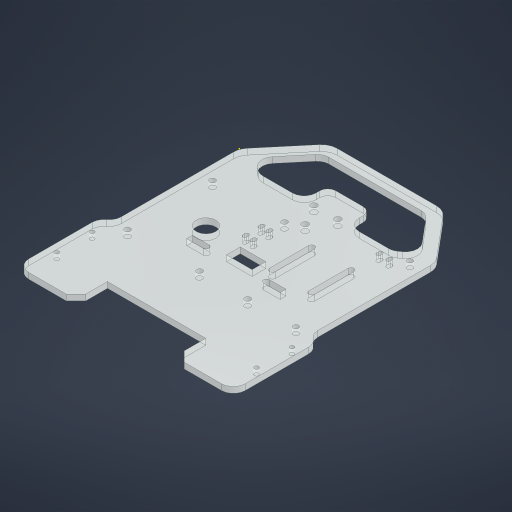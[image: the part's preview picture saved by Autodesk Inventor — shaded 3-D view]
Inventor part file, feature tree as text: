
AUTODESK INVENTOR PART (.ipt)
format: ipt  version: 2023 (Build 270158000, 158)  size: 454,656 bytes
history: native  units: mm
features: sketch x3, extrude x2, fillet x1, chamfer x1
ambient origin geometry x8: Origin, YZ Plane, XZ Plane, XY Plane, X Axis, Y Axis, Z Axis, Center Point
bodies: Solid1 (feature_tree)
feature tree (7):
  extrude  "Extrusion1"  Depth=100.0mm
  fillet  "Fillet1"  Radius=8.0mm
  sketch  "Sketch2"  dims[d4=2.2mm d5=18.0mm]
  extrude  "Extrusion2"  Depth=18.0mm
  chamfer  "Chamfer2"  Distance=36.576mm
  sketch  "Sketch1"  dims[d0=100.0mm d1=100.0mm d2=8.0mm]
  sketch  "Sketch3"  dims[d6=43.18mm d7=36.576mm d8=3.0mm d9=49.0mm d10=58.0mm d15=2.75mm d27=3.0mm d28=0.0mm d33=22.0mm d34=25.0mm d36=22.68928mm d37=6.0mm d38=6.0mm d39=12.0mm d40=6.0mm d41=8.0mm d44=2.3mm d45=13.462mm d46=5.0mm d47=14.0mm d48=15.5mm d49=3.3mm d54=4.0mm d55=5.0mm d56=34.0mm d57=4.25mm d58=6.0mm d59=30.0mm d60=8.0mm d61=8.0mm d62=30.0mm d64=360.0deg d66=3.0mm d67=18.0mm d68=20.0mm d69=20.0mm d71=20.0mm d72=10.0mm d74=10.0mm d76=1.0mm d77=2.0mm d78=4.0mm d79=20.0mm d81=5.0mm d82=10.0mm d84=10.0mm d86=1.0mm d87=2.0mm d88=20.0mm d90=4.0mm d91=10.0mm d93=10.0mm d95=20.0mm d97=8.0mm d98=10.0mm d100=10.0mm d102=27.0mm d103=3.0mm d104=0.0mm d105=5.0mm d106=2.0mm d107=45.0deg d108=10.0mm d109=3.0mm d110=47.5mm d111=3.0mm d113=11.0mm d114=0.0mm d115=13.0mm d116=6.9mm d117=7.0mm]
